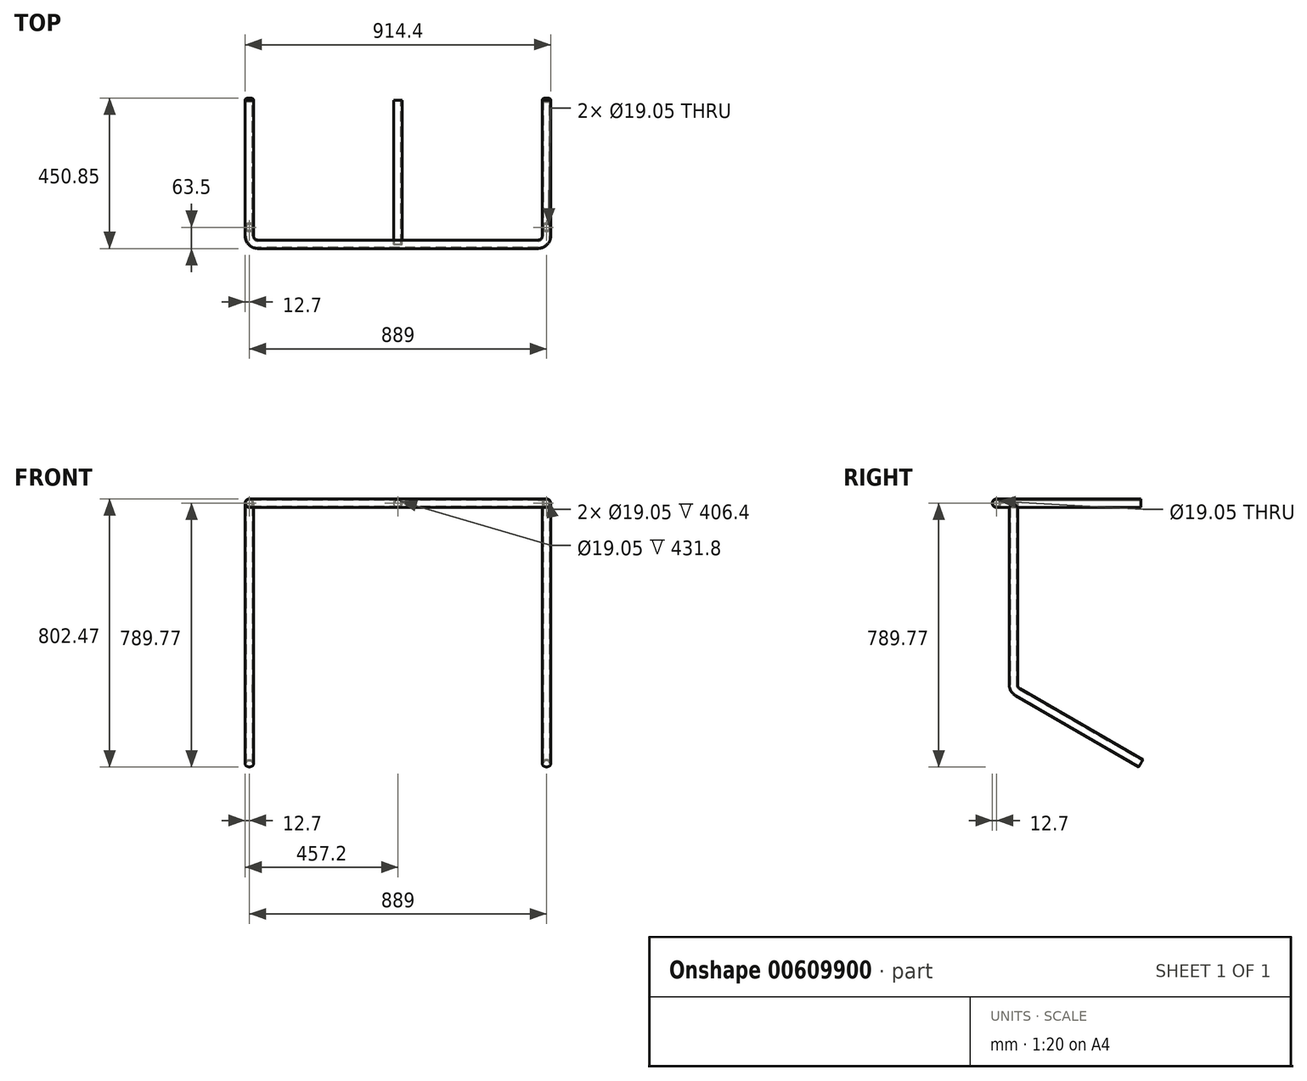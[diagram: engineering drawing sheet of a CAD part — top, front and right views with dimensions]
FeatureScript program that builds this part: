
annotation { "Feature Type Name" : "Feature", "Feature Type Description" : "" }
export const myFeature = defineFeature(function(context is Context, id is Id, definition is map)
    precondition{}
    {
        {
            var Q0;
            Q0=qCreatedBy(makeId("Top.planeOp"),FACE);
            var sketch = newSketch(context, id + "F0", { "sketchPlane" : qUnion([Q0])});
            skLineSegment(sketch, "E0", {"start": v(-444.5, 431.8) * mm, "end": v(-444.5, 25.4) * mm});
            skLineSegment(sketch, "E1", {"start": v(-419.1, 0) * mm, "end": v(419.1, 0) * mm});
            skLineSegment(sketch, "E2", {"start": v(444.5, 431.8) * mm, "end": v(444.5, 25.4) * mm});
            skLineSegment(sketch, "E3", {"start": v(0, 431.8) * mm, "end": v(0, 0) * mm});
            skArc(sketch, "E4", {"start": v(-444.5, 25.4) * mm, "mid": v(-437.06, 7.44) * mm, "end": v(-419.1, 0) * mm});
            skPoint(sketch, "E5.orphan", {"position": v(-444.5, 0) * mm});
            skArc(sketch, "E6", {"start": v(419.1, 0) * mm, "mid": v(437.06, 7.44) * mm, "end": v(444.5, 25.4) * mm});
            skPoint(sketch, "E7.orphan", {"position": v(444.5, 0) * mm});
            skSolve(sketch);
        }
        {
            var Q0;
            Q0=qCreatedBy(makeId("Front.planeOp"),FACE);
            cPlane(context, id + "F1", {"entities" : qUnion([Q0]), "cplaneType" : CPlaneType.OFFSET, "offset" : 431.8 * mm, "oppositeDirection" : true, "width" : 152.4 * mm, "height" : 152.4 * mm});
        }
        {
            var Q0;
            Q0=qCreatedBy(id+"F1.planeOp",FACE);
            var sketch = newSketch(context, id + "F2", { "sketchPlane" : qUnion([Q0])});
            skCircle(sketch, "E8", {"center": v(444.5, 0) * mm, "radius": 12.7 * mm});
            skCircle(sketch, "E9", {"center": v(444.5, 0) * mm, "radius": 9.53 * mm});
            skSolve(sketch);
        }
        {
            var Q0;
            Q0=makeQuery(id+"F2.imprint","IMPRINT",FACE,{"disambiguationData":[TD([[makeQuery(id+"F2.imprint","IMPRINT",EDGE,{"derivedFrom":sQuery(id+"F2.wireOp",EDGE,"E8")}),1.0]])]});
            var Q1;
            Q1=sQuery(id+"F0.wireOp",EDGE,"E2");
            var Q2;
            Q2=sQuery(id+"F0.wireOp",EDGE,"E1");
            var Q3;
            Q3=sQuery(id+"F0.wireOp",EDGE,"E0");
            var Q4;
            Q4=sQuery(id+"F0.wireOp",EDGE,"E4");
            var Q5;
            Q5=sQuery(id+"F0.wireOp",EDGE,"E6");
            sweep(context, id + "F3", {"profiles" : qUnion([Q0]), "path" : qUnion([Q1, Q2, Q3, Q4, Q5])});
        }
        {
            var Q0;
            Q0=qCreatedBy(makeId("Front.planeOp"),FACE);
            var sketch = newSketch(context, id + "F4", { "sketchPlane" : qUnion([Q0])});
            skCircle(sketch, "E10", {"center": v(0, 0) * mm, "radius": 12.7 * mm});
            skCircle(sketch, "E11", {"center": v(0, 0) * mm, "radius": 9.53 * mm});
            skSolve(sketch);
        }
        {
            var Q0;
            Q0=makeQuery(id+"F4.imprint","IMPRINT",FACE,{"disambiguationData":[TD([[makeQuery(id+"F4.imprint","IMPRINT",EDGE,{"derivedFrom":sQuery(id+"F4.wireOp",EDGE,"E10")}),1.0]])]});
            var Q1;
            Q1=sQuery(id+"F0.wireOp",EDGE,"E3");
            sweep(context, id + "F5", {"profiles" : qUnion([Q0]), "path" : qUnion([Q1])});
        }
        {
            var Q0;
            Q0=qCreatedBy(makeId("Top.planeOp"),FACE);
            var sketch = newSketch(context, id + "F6", { "sketchPlane" : qUnion([Q0])});
            skCircle(sketch, "E12", {"center": v(444.5, 50.8) * mm, "radius": 12.7 * mm});
            skCircle(sketch, "E13", {"center": v(-444.5, 50.8) * mm, "radius": 12.7 * mm});
            skCircle(sketch, "E14", {"center": v(444.5, 50.8) * mm, "radius": 9.53 * mm});
            skCircle(sketch, "E15", {"center": v(-444.5, 50.8) * mm, "radius": 9.53 * mm});
            skSolve(sketch);
        }
        {
            var Q0;
            Q0=qCreatedBy(makeId("Right.planeOp"),FACE);
            cPlane(context, id + "F7", {"entities" : qUnion([Q0]), "cplaneType" : CPlaneType.OFFSET, "offset" : 444.5 * mm, "width" : 152.4 * mm, "height" : 152.4 * mm});
        }
        {
            var Q0;
            Q0=qCreatedBy(id+"F7.planeOp",FACE);
            var sketch = newSketch(context, id + "F8", { "sketchPlane" : qUnion([Q0])});
            skLineSegment(sketch, "E16", {"start": v(50.8, 0) * mm, "end": v(50.8, -544.14) * mm});
            skLineSegment(sketch, "E17", {"start": v(63.5, -566.13) * mm, "end": v(431.8, -778.77) * mm});
            skArc(sketch, "E18", {"start": v(50.8, -544.14) * mm, "mid": v(54.2, -556.84) * mm, "end": v(63.5, -566.13) * mm});
            skSolve(sketch);
        }
        {
            var Q0;
            Q0=makeQuery(id+"F6.imprint","IMPRINT",FACE,{"disambiguationData":[TD([[makeQuery(id+"F6.imprint","IMPRINT",EDGE,{"derivedFrom":sQuery(id+"F6.wireOp",EDGE,"E12")}),1.0]])]});
            var Q1;
            Q1=sQuery(id+"F8.wireOp",EDGE,"E16");
            var Q2;
            Q2=sQuery(id+"F8.wireOp",EDGE,"E18");
            var Q3;
            Q3=sQuery(id+"F8.wireOp",EDGE,"E17");
            sweep(context, id + "F9", {"profiles" : qUnion([Q0]), "path" : qUnion([Q1, Q2, Q3])});
        }
        {
            var Q0;
            Q0=makeQuery(id+"F9.opSweep","SWEPT_BODY",BODY,{"disambiguationData":[OSD([sQuery(id+"F6.wireOp",EDGE,"E12"),sQuery(id+"F6.wireOp",EDGE,"E14"),sQuery(id+"F8.wireOp",EDGE,"E17")])]});
            var Q1;
            Q1=qCreatedBy(makeId("Right.planeOp"),FACE);
            mirror(context, id + "F10", {"operationType" : NewBodyOperationType.ADD, "entities" : qUnion([Q0]), "mirrorPlane" : qUnion([Q1])});
        }
    });
